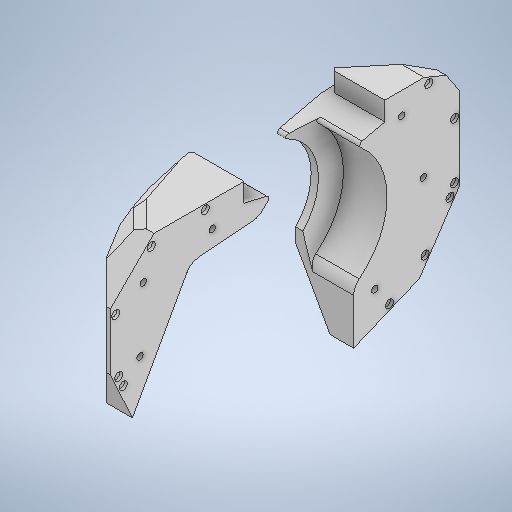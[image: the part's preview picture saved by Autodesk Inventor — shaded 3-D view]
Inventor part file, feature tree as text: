
AUTODESK INVENTOR PART (.ipt)
format: ipt  version: 2025.2 (Build 292293000, 293)  size: 751,616 bytes
history: native  units: in
note: dims shown in document units (in); Inventor stores cm internally (conversion verified against a paired STEP export)
features: other x2, extrude x1, sketch x1
ambient origin geometry x8: Origin, YZ Plane, XZ Plane, XY Plane, X Axis, Y Axis, Z Axis, Center Point
bodies: body_side (feature_tree)
feature tree (4):
  extrude  "Extrusion1"  Depth=0.2362in
  other  "Solid2::body_side"
  other  "TaggingFeature1"
  sketch  "Sketch1"  dims[d0=0.3937in d1=0.1752in d2=0.1752in d3=0.1752in d6=0.1752in d7=0.1752in d8=0.1752in d9=0.2362in d10=0.0in]
